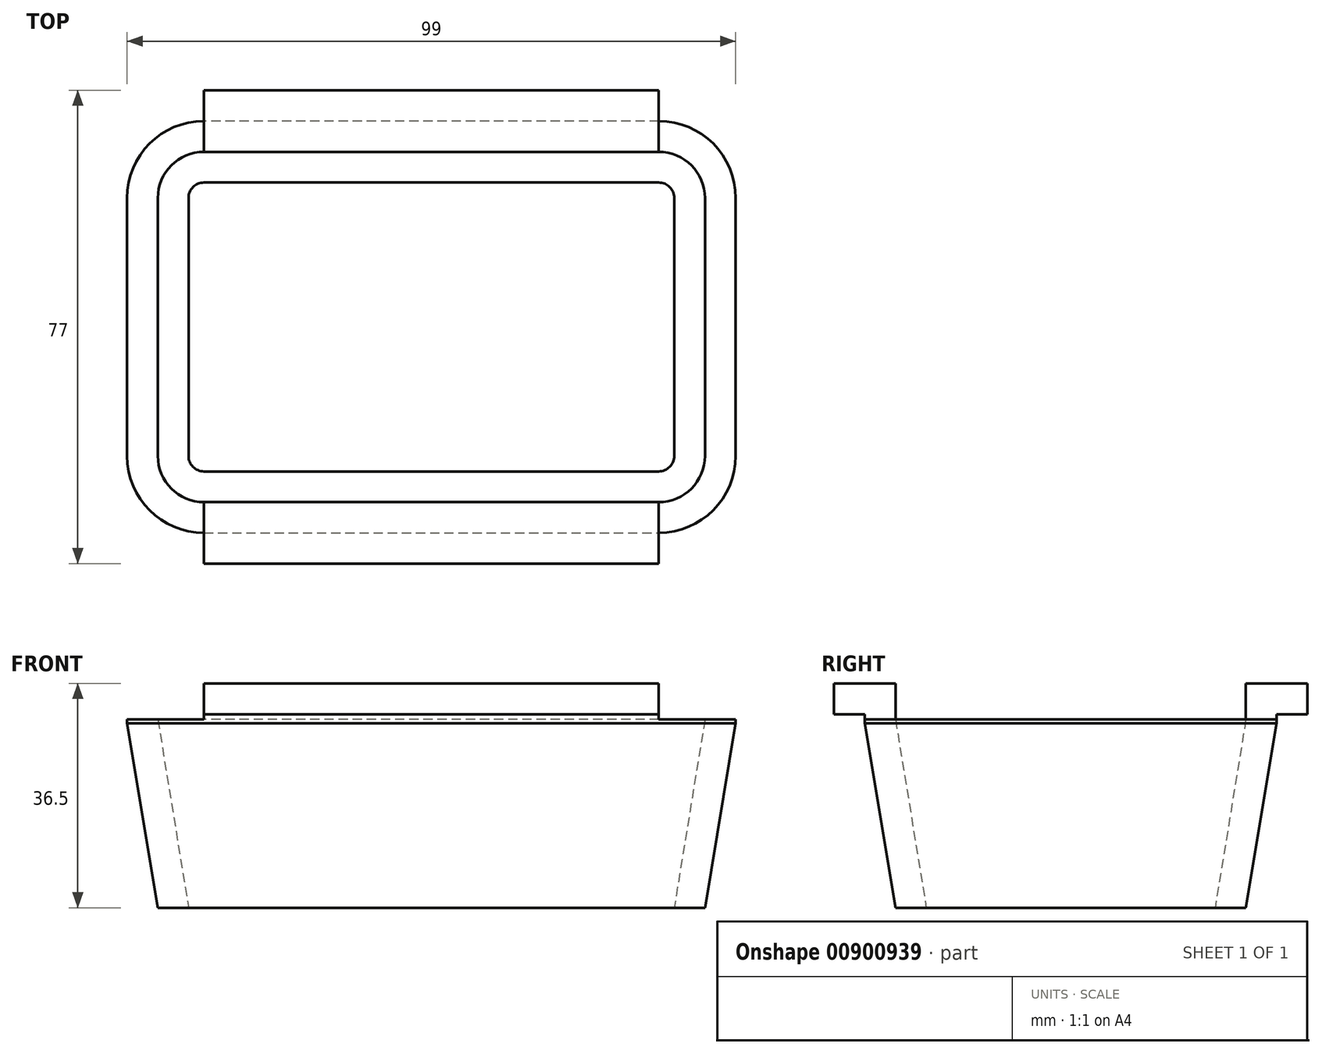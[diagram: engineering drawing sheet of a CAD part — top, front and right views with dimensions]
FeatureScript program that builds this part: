
annotation { "Feature Type Name" : "Feature", "Feature Type Description" : "" }
export const myFeature = defineFeature(function(context is Context, id is Id, definition is map)
    precondition{}
    {
        {
            var Q0;
            Q0=qCreatedBy(makeId("Top.planeOp"),FACE);
            var sketch = newSketch(context, id + "F0", { "sketchPlane" : qUnion([Q0])});
            skPoint(sketch, "E0.middle", {"position": v(0, 0) * mm});
            skPoint(sketch, "E1", {"position": v(37, 21) * mm});
            skPoint(sketch, "E2", {"position": v(-37, -21) * mm});
            skPoint(sketch, "E3", {"position": v(-37, 21) * mm});
            skArc(sketch, "E4", {"start": v(-49.5, -21) * mm, "mid": v(-45.84, -29.84) * mm, "end": v(-37, -33.5) * mm});
            skArc(sketch, "E5", {"start": v(-37, 33.5) * mm, "mid": v(-45.84, 29.84) * mm, "end": v(-49.5, 21) * mm});
            skArc(sketch, "E6", {"start": v(37, -33.5) * mm, "mid": v(45.84, -29.84) * mm, "end": v(49.5, -21) * mm});
            skArc(sketch, "E7", {"start": v(49.5, 21) * mm, "mid": v(45.84, 29.84) * mm, "end": v(37, 33.5) * mm});
            skLineSegment(sketch, "E8", {"start": v(49.5, -21) * mm, "end": v(49.5, 21) * mm});
            skLineSegment(sketch, "E9", {"start": v(-37, -33.5) * mm, "end": v(37, -33.5) * mm});
            skLineSegment(sketch, "E10", {"start": v(-49.5, -21) * mm, "end": v(-49.5, 21) * mm});
            skLineSegment(sketch, "E11", {"start": v(-37, 33.5) * mm, "end": v(37, 33.5) * mm});
            skSolve(sketch);
        }
        {
            var Q0;
            Q0=qCreatedBy(makeId("Front.planeOp"),FACE);
            var sketch = newSketch(context, id + "F1", { "sketchPlane" : qUnion([Q0])});
            skLineSegment(sketch, "E12.top", {"start": v(-44.5, -30) * mm, "end": v(-39.5, -30) * mm});
            skLineSegment(sketch, "E13", {"start": v(-49.5, 0) * mm, "end": v(-44.5, -30) * mm});
            skLineSegment(sketch, "E14", {"start": v(-44.5, 0.62) * mm, "end": v(-39.5, -30) * mm});
            skPoint(sketch, "E15.orphan", {"position": v(-49.5, -30) * mm});
            skLineSegment(sketch, "E16.left", {"start": v(-49.5, 0) * mm, "end": v(-49.5, 1.5) * mm});
            skLineSegment(sketch, "E16.right", {"start": v(-44.5, 0) * mm, "end": v(-44.5, 6.5) * mm});
            skLineSegment(sketch, "E17.top", {"start": v(-49.5, 1.5) * mm, "end": v(-54.5, 1.5) * mm});
            skLineSegment(sketch, "E17.right", {"start": v(-54.5, 6.5) * mm, "end": v(-54.5, 1.5) * mm});
            skLineSegment(sketch, "E18", {"start": v(-54.5, 6.5) * mm, "end": v(-44.5, 6.5) * mm});
            skSolve(sketch);
        }
        {
            var Q0;
            Q0=makeQuery(id+"F1.imprint","IMPRINT",FACE,{"disambiguationData":[TD([[makeQuery(id+"F1.imprint","IMPRINT",EDGE,{"derivedFrom":sQuery(id+"F1.wireOp",EDGE,"E12.top")}),1.0]])]});
            var Q1;
            Q1=sQuery(id+"F0.wireOp",EDGE,"E10");
            var Q2;
            Q2=sQuery(id+"F0.wireOp",EDGE,"E5");
            var Q3;
            Q3=sQuery(id+"F0.wireOp",EDGE,"E11");
            var Q4;
            Q4=sQuery(id+"F0.wireOp",EDGE,"E4");
            var Q5;
            Q5=sQuery(id+"F0.wireOp",EDGE,"E9");
            var Q6;
            Q6=sQuery(id+"F0.wireOp",EDGE,"E6");
            var Q7;
            Q7=sQuery(id+"F0.wireOp",EDGE,"E8");
            var Q8;
            Q8=sQuery(id+"F0.wireOp",EDGE,"E7");
            sweep(context, id + "F2", {"profiles" : qUnion([Q0]), "path" : qUnion([Q1, Q2, Q3, Q4, Q5, Q6, Q7, Q8])});
        }
        {
            var Q0;
            Q0=makeQuery(id+"F2.opSweep","SWEPT_FACE",FACE,{"disambiguationData":[OSD([sQuery(id+"F0.wireOp",EDGE,"E10"),sQuery(id+"F1.wireOp",EDGE,"E18")])]});
            var sketch = newSketch(context, id + "F3", { "sketchPlane" : qUnion([Q0])});
            skLineSegment(sketch, "E19", {"start": v(-37, -38.5) * mm, "end": v(-37, -28.5) * mm});
            skLineSegment(sketch, "E20", {"start": v(-37, 28.5) * mm, "end": v(-37, 38.5) * mm});
            skSolve(sketch);
        }
        {
            var Q0;
            Q0=qSketchRegion(id+"F3",true);
            var Q1;
            Q1=makeQuery(id+"F3.imprint","IMPRINT",FACE,{"disambiguationData":[TD([[makeQuery(id+"F3.imprint","IMPRINT",EDGE,{"derivedFrom":sQuery(id+"F3.wireOp",EDGE,"E19")}),1.0]])]});
            extrude(context, id + "F4", {"entities" : qUnion([Q0, Q1]), "operationType" : NewBodyOperationType.REMOVE, "oppositeDirection" : true, "depth" : 5.88 * mm, "offsetDistance" : 25 * mm});
        }
        {
            var Q0;
            Q0=makeQuery(id+"F2.opSweep","SWEPT_FACE",FACE,{"disambiguationData":[OSD([sQuery(id+"F0.wireOp",EDGE,"E10"),sQuery(id+"F1.wireOp",EDGE,"E18")])]});
            var sketch = newSketch(context, id + "F5", { "sketchPlane" : qUnion([Q0])});
            skLineSegment(sketch, "E21", {"start": v(37, -38.5) * mm, "end": v(37, -28.5) * mm});
            skLineSegment(sketch, "E22", {"start": v(37, 28.5) * mm, "end": v(37, 38.5) * mm});
            skSolve(sketch);
        }
        {
            var Q0;
            Q0=qSketchRegion(id+"F5",true);
            var Q1;
            Q1=makeQuery(id+"F5.imprint","IMPRINT",FACE,{"disambiguationData":[TD([[makeQuery(id+"F5.imprint","IMPRINT",EDGE,{"derivedFrom":sQuery(id+"F5.wireOp",EDGE,"E21")}),-1.0]])]});
            extrude(context, id + "F6", {"entities" : qUnion([Q0, Q1]), "operationType" : NewBodyOperationType.REMOVE, "oppositeDirection" : true, "depth" : 5.88 * mm, "offsetDistance" : 25 * mm});
        }
    });
